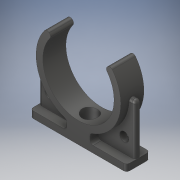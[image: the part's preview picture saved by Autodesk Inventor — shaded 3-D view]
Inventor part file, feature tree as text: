
AUTODESK INVENTOR PART (.ipt)
format: ipt  version: 2018.3 (Build 223284000, 284)  size: 189,440 bytes
history: native  units: in
note: dims shown in document units (in); Inventor stores cm internally (conversion verified against a paired STEP export)
features: fillet x1
ambient origin geometry x8: Origin, YZ Plane, XZ Plane, XY Plane, X Axis, Y Axis, Z Axis, Center Point
bodies: Solid1 (feature_tree)
feature tree (1):
  fillet  "Fillet3"  [1 undecoded]
note: 1 required parameter value undecoded (feature->parameter linkage not recoverable at this tier; creation-order binding heuristic only, values carry confidence <= 0.55)
